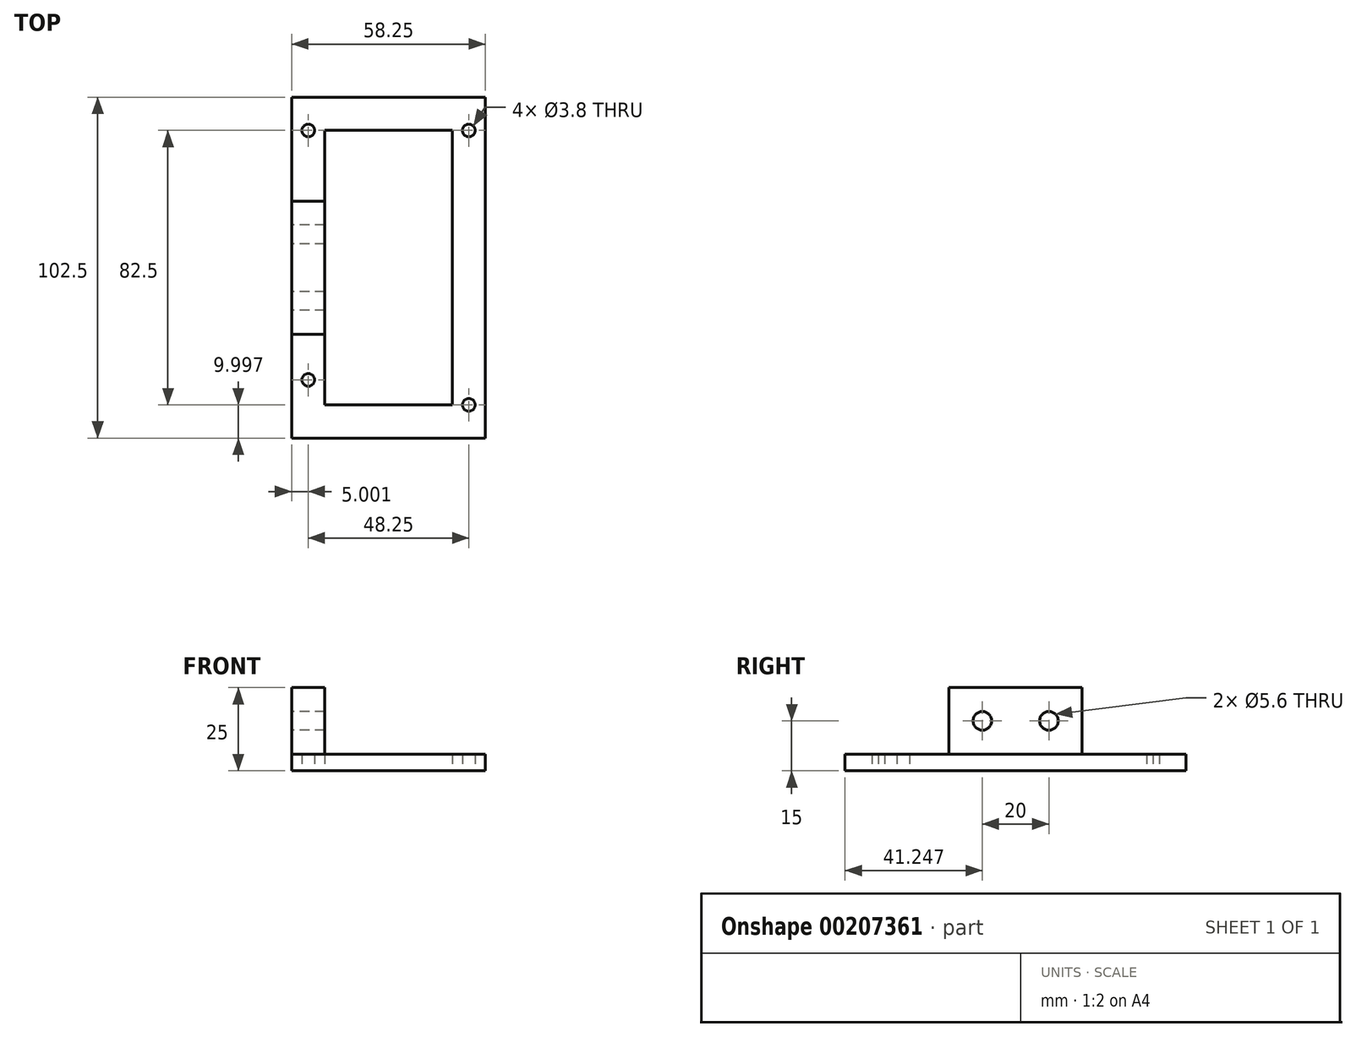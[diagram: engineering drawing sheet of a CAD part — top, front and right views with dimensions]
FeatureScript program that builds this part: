
annotation { "Feature Type Name" : "Feature", "Feature Type Description" : "" }
export const myFeature = defineFeature(function(context is Context, id is Id, definition is map)
    precondition{}
    {
        {
            var Q0;
            Q0=qCreatedBy(makeId("Top.planeOp"),FACE);
            var sketch = newSketch(context, id + "F0", { "sketchPlane" : qUnion([Q0])});
            skLineSegment(sketch, "E0.bottom", {"start": v(-37.26, 38.98) * mm, "end": v(21, 38.98) * mm});
            skLineSegment(sketch, "E0.top", {"start": v(-37.26, -63.52) * mm, "end": v(21, -63.52) * mm});
            skLineSegment(sketch, "E0.left", {"start": v(-37.26, 38.98) * mm, "end": v(-37.26, -63.52) * mm});
            skLineSegment(sketch, "E0.right", {"start": v(21, 38.98) * mm, "end": v(21, -63.52) * mm});
            skLineSegment(sketch, "E1.0", {"start": v(11, 28.98) * mm, "end": v(11, -53.52) * mm});
            skLineSegment(sketch, "E1.1", {"start": v(-27.26, 28.98) * mm, "end": v(11, 28.98) * mm});
            skLineSegment(sketch, "E1.2", {"start": v(-27.26, 28.98) * mm, "end": v(-27.26, -53.52) * mm});
            skLineSegment(sketch, "E1.3", {"start": v(-27.26, -53.52) * mm, "end": v(11, -53.52) * mm});
            skCircle(sketch, "E2", {"center": v(-32.26, 28.98) * mm, "radius": 1.9 * mm});
            skCircle(sketch, "E3", {"center": v(-32.26, -46.02) * mm, "radius": 1.9 * mm});
            skCircle(sketch, "E4", {"center": v(16, 28.98) * mm, "radius": 1.9 * mm});
            skCircle(sketch, "E5", {"center": v(16, -53.52) * mm, "radius": 1.9 * mm});
            skLineSegment(sketch, "E6", {"start": v(-27.26, 28.98) * mm, "end": v(-37.26, 28.98) * mm, "construction": true});
            skLineSegment(sketch, "E7", {"start": v(11, 28.98) * mm, "end": v(21, 28.98) * mm, "construction": true});
            skLineSegment(sketch, "E8", {"start": v(-37.26, 7.73) * mm, "end": v(-27.26, 7.73) * mm});
            skLineSegment(sketch, "E9", {"start": v(-37.26, -32.27) * mm, "end": v(-27.26, -32.27) * mm});
            skPoint(sketch, "E10", {"position": v(-37.26, -12.27) * mm});
            skSolve(sketch);
        }
        {
            var Q0;
            {var subQ7=sQuery(id+"F0.wireOp",EDGE,"E0.bottom");Q0=makeQuery(id+"F0.imprint","IMPRINT",FACE,{"disambiguationData":[TD([[makeQuery(id+"F0.imprint","IMPRINT",EDGE,{"derivedFrom":subQ7}),-1.0]])]});}
            extrude(context, id + "F1", {"entities" : qUnion([Q0]), "depth" : 5 * mm});
        }
        {
            var Q0;
            {var subQ1=sQuery(id+"F0.wireOp",EDGE,"E8");Q0=makeQuery(id+"F0.imprint","IMPRINT",FACE,{"disambiguationData":[TD([[makeQuery(id+"F0.imprint","IMPRINT",EDGE,{"derivedFrom":subQ1}),-1.0]])]});}
            extrude(context, id + "F2", {"entities" : qUnion([Q0]), "operationType" : NewBodyOperationType.ADD, "depth" : 25 * mm});
        }
        {
            var Q0;
            {var subQ0=sQuery(id+"F0.wireOp",EDGE,"E0.left");Q0=makeQuery(id+"F2.boolean.opBoolean","MERGE",FACE,{"derivedFrom":[makeQuery(id+"F1.opExtrude","SWEPT_FACE",FACE,{"disambiguationData":[OSD([subQ0]),TDD([makeQuery(id+"F0.imprint","IMPRINT",EDGE,{"disambiguationData":[TD([[makeQuery(id+"F0.imprint","INTERSECT",VERTEX,{"derivedFrom":[sQuery(id+"F0.wireOp",EDGE,"E0.bottom"),subQ0]}),-1.0]])],"derivedFrom":subQ0})])]}),makeQuery(id+"F1.opExtrude","SWEPT_FACE",FACE,{"disambiguationData":[OSD([subQ0]),TDD([makeQuery(id+"F0.imprint","IMPRINT",EDGE,{"disambiguationData":[TD([[makeQuery(id+"F0.imprint","INTERSECT",VERTEX,{"derivedFrom":[sQuery(id+"F0.wireOp",EDGE,"E0.top"),subQ0]}),1.0]])],"derivedFrom":subQ0})])]}),makeQuery(id+"F2.opExtrude","SWEPT_FACE",FACE,{"disambiguationData":[OSD([subQ0])]})]});}
            var sketch = newSketch(context, id + "F3", { "sketchPlane" : qUnion([Q0])});
            skPoint(sketch, "E11", {"position": v(32.27, 15) * mm});
            skPoint(sketch, "E12.0", {"position": v(12.27, 0) * mm});
            skCircle(sketch, "E13", {"center": v(22.27, 15) * mm, "radius": 2.8 * mm});
            skCircle(sketch, "E14", {"center": v(2.27, 15) * mm, "radius": 2.8 * mm});
            skSolve(sketch);
        }
        {
            var Q0;
            Q0=makeQuery(id+"F3.imprint","IMPRINT",FACE,{"disambiguationData":[TD([[makeQuery(id+"F3.imprint","IMPRINT",EDGE,{"derivedFrom":sQuery(id+"F3.wireOp",EDGE,"E14")}),1.0]])]});
            var Q1;
            Q1=makeQuery(id+"F3.imprint","IMPRINT",FACE,{"disambiguationData":[TD([[makeQuery(id+"F3.imprint","IMPRINT",EDGE,{"derivedFrom":sQuery(id+"F3.wireOp",EDGE,"E13")}),1.0]])]});
            var Q2;
            {var subQ0=sQuery(id+"F0.wireOp",EDGE,"E1.2");Q2=makeQuery(id+"F2.boolean.opBoolean","MERGE",FACE,{"derivedFrom":[makeQuery(id+"F1.opExtrude","SWEPT_FACE",FACE,{"disambiguationData":[OSD([subQ0]),TDD([makeQuery(id+"F0.imprint","IMPRINT",EDGE,{"disambiguationData":[TD([[makeQuery(id+"F0.imprint","INTERSECT",VERTEX,{"derivedFrom":[sQuery(id+"F0.wireOp",EDGE,"E1.1"),subQ0]}),-1.0]])],"derivedFrom":subQ0})])]}),makeQuery(id+"F1.opExtrude","SWEPT_FACE",FACE,{"disambiguationData":[OSD([subQ0]),TDD([makeQuery(id+"F0.imprint","IMPRINT",EDGE,{"disambiguationData":[TD([[makeQuery(id+"F0.imprint","INTERSECT",VERTEX,{"derivedFrom":[subQ0,sQuery(id+"F0.wireOp",EDGE,"E1.3")]}),1.0]])],"derivedFrom":subQ0})])]}),makeQuery(id+"F2.opExtrude","SWEPT_FACE",FACE,{"disambiguationData":[OSD([subQ0])]})]});}
            extrude(context, id + "F4", {"entities" : qUnion([Q0, Q1]), "operationType" : NewBodyOperationType.REMOVE, "endBound" : BoundingType.UP_TO_SURFACE, "oppositeDirection" : true, "endBoundEntityFace" : qUnion([Q2]), "depth" : 25 * mm});
        }
    });
